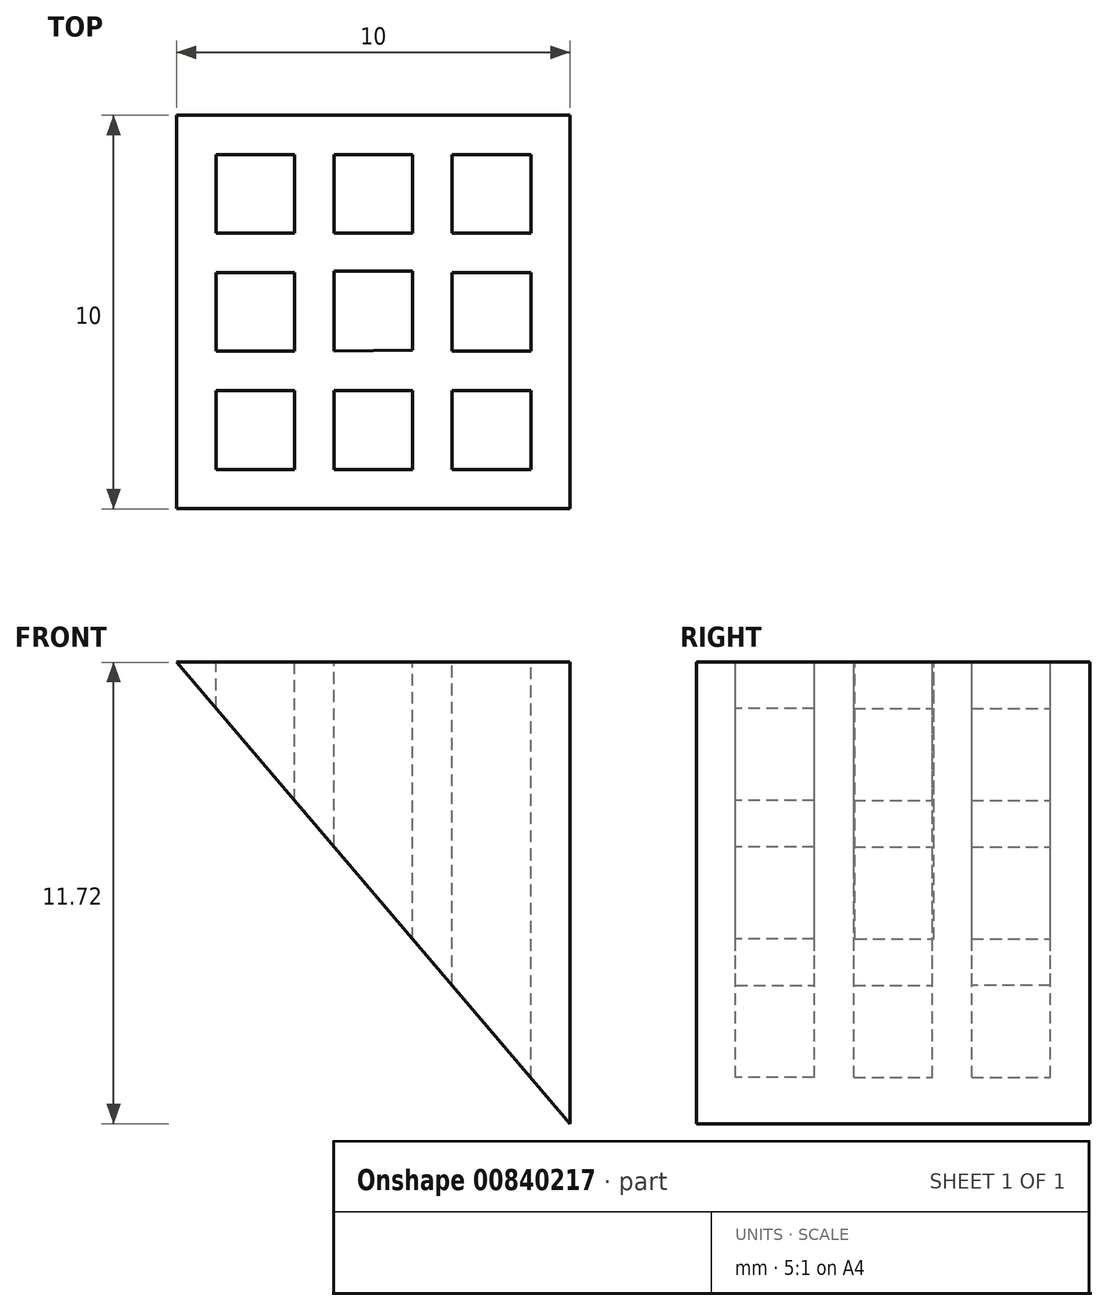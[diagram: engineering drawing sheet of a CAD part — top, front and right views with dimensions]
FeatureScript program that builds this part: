
annotation { "Feature Type Name" : "Feature", "Feature Type Description" : "" }
export const myFeature = defineFeature(function(context is Context, id is Id, definition is map)
    precondition{}
    {
        {
            var Q0;
            Q0=qCreatedBy(makeId("Top.planeOp"),FACE);
            var sketch = newSketch(context, id + "F0", { "sketchPlane" : qUnion([Q0])});
            skLineSegment(sketch, "E0", {"start": v(-23.24, 8.4) * mm, "end": v(-23.24, -1.6) * mm});
            skLineSegment(sketch, "E1", {"start": v(-23.24, 8.4) * mm, "end": v(-13.24, 8.4) * mm});
            skLineSegment(sketch, "E2", {"start": v(-23.24, -1.6) * mm, "end": v(-13.24, -1.6) * mm});
            skLineSegment(sketch, "E3", {"start": v(-13.24, 8.4) * mm, "end": v(-13.24, -1.6) * mm});
            skSolve(sketch);
        }
        {
            var Q0;
            Q0=makeQuery(id+"F0.imprint","IMPRINT",FACE,{"disambiguationData":[TD([[makeQuery(id+"F0.imprint","IMPRINT",EDGE,{"derivedFrom":sQuery(id+"F0.wireOp",EDGE,"E0")}),1.0]])]});
            extrude(context, id + "F1", {"entities" : qUnion([Q0]), "depth" : 577 * mm, "offsetDistance" : 25 * mm});
        }
        {
            var Q0;
            Q0=makeQuery(id+"F1.opExtrude","CAP_FACE",FACE,{"disambiguationData":[OSD([sQuery(id+"F0.wireOp",EDGE,"E0"),sQuery(id+"F0.wireOp",EDGE,"E1"),sQuery(id+"F0.wireOp",EDGE,"E2"),sQuery(id+"F0.wireOp",EDGE,"E3")])],"isStart":false});
            var sketch = newSketch(context, id + "F2", { "sketchPlane" : qUnion([Q0])});
            skLineSegment(sketch, "E4", {"start": v(-22.24, 7.4) * mm, "end": v(-22.24, 5.4) * mm});
            skLineSegment(sketch, "E5", {"start": v(-22.24, 7.4) * mm, "end": v(-20.24, 7.4) * mm});
            skLineSegment(sketch, "E6", {"start": v(-22.24, 5.4) * mm, "end": v(-20.24, 5.4) * mm});
            skLineSegment(sketch, "E7", {"start": v(-20.24, 7.4) * mm, "end": v(-20.24, 5.4) * mm});
            skLineSegment(sketch, "E8", {"start": v(-19.24, 7.4) * mm, "end": v(-19.24, 5.4) * mm});
            skLineSegment(sketch, "E9", {"start": v(-19.24, 5.4) * mm, "end": v(-17.24, 5.4) * mm});
            skLineSegment(sketch, "E10", {"start": v(-19.24, 7.4) * mm, "end": v(-17.24, 7.4) * mm});
            skLineSegment(sketch, "E11", {"start": v(-17.24, 7.4) * mm, "end": v(-17.24, 5.4) * mm});
            skLineSegment(sketch, "E12", {"start": v(-16.24, 5.4) * mm, "end": v(-16.24, 7.4) * mm});
            skLineSegment(sketch, "E13", {"start": v(-16.24, 5.4) * mm, "end": v(-14.24, 5.4) * mm});
            skLineSegment(sketch, "E14", {"start": v(-16.24, 7.4) * mm, "end": v(-14.24, 7.4) * mm});
            skLineSegment(sketch, "E15", {"start": v(-14.24, 7.4) * mm, "end": v(-14.24, 5.4) * mm});
            skLineSegment(sketch, "E16", {"start": v(-12.45, 8.4) * mm, "end": v(-12.45, 3.4) * mm});
            skLineSegment(sketch, "E17.MirrorCS", {"start": v(-19.24, 1.4) * mm, "end": v(-17.24, 1.4) * mm});
            skLineSegment(sketch, "E18.MirrorCS", {"start": v(-19.24, -0.6) * mm, "end": v(-19.24, 1.4) * mm});
            skLineSegment(sketch, "E19.MirrorCS", {"start": v(-19.24, -0.6) * mm, "end": v(-17.24, -0.6) * mm});
            skLineSegment(sketch, "E20.MirrorCS", {"start": v(-17.24, -0.6) * mm, "end": v(-17.24, 1.4) * mm});
            skLineSegment(sketch, "E21.MirrorCS", {"start": v(-16.24, 1.4) * mm, "end": v(-14.24, 1.4) * mm});
            skLineSegment(sketch, "E22.MirrorCS", {"start": v(-16.24, 1.4) * mm, "end": v(-16.24, -0.6) * mm});
            skLineSegment(sketch, "E23.MirrorCS", {"start": v(-14.24, -0.6) * mm, "end": v(-14.24, 1.4) * mm});
            skLineSegment(sketch, "E24.MirrorCS", {"start": v(-16.24, -0.6) * mm, "end": v(-14.24, -0.6) * mm});
            skLineSegment(sketch, "E25.MirrorCS", {"start": v(-22.24, 1.4) * mm, "end": v(-20.24, 1.4) * mm});
            skLineSegment(sketch, "E26.MirrorCS", {"start": v(-22.24, -0.6) * mm, "end": v(-22.24, 1.4) * mm});
            skLineSegment(sketch, "E27.MirrorCS", {"start": v(-22.24, -0.6) * mm, "end": v(-20.24, -0.6) * mm});
            skLineSegment(sketch, "E28.MirrorCS", {"start": v(-20.24, -0.6) * mm, "end": v(-20.24, 1.4) * mm});
            skSolve(sketch);
        }
        {
            var Q0;
            Q0=makeQuery(id+"F2.imprint","IMPRINT",FACE,{"disambiguationData":[TD([[makeQuery(id+"F2.imprint","IMPRINT",EDGE,{"derivedFrom":sQuery(id+"F2.wireOp",EDGE,"E4")}),1.0]])]});
            var Q1;
            Q1=makeQuery(id+"F2.imprint","IMPRINT",FACE,{"disambiguationData":[TD([[makeQuery(id+"F2.imprint","IMPRINT",EDGE,{"derivedFrom":sQuery(id+"F2.wireOp",EDGE,"E8")}),1.0]])]});
            var Q2;
            Q2=makeQuery(id+"F2.imprint","IMPRINT",FACE,{"disambiguationData":[TD([[makeQuery(id+"F2.imprint","IMPRINT",EDGE,{"derivedFrom":sQuery(id+"F2.wireOp",EDGE,"E12")}),-1.0]])]});
            var Q3;
            Q3=makeQuery(id+"F2.imprint","IMPRINT",FACE,{"disambiguationData":[TD([[makeQuery(id+"F2.imprint","IMPRINT",EDGE,{"derivedFrom":sQuery(id+"F2.wireOp",EDGE,"E21.MirrorCS")}),-1.0]])]});
            var Q4;
            Q4=makeQuery(id+"F2.imprint","IMPRINT",FACE,{"disambiguationData":[TD([[makeQuery(id+"F2.imprint","IMPRINT",EDGE,{"derivedFrom":sQuery(id+"F2.wireOp",EDGE,"E17.MirrorCS")}),-1.0]])]});
            var Q5;
            Q5=makeQuery(id+"F2.imprint","IMPRINT",FACE,{"disambiguationData":[TD([[makeQuery(id+"F2.imprint","IMPRINT",EDGE,{"derivedFrom":sQuery(id+"F2.wireOp",EDGE,"E25.MirrorCS")}),-1.0]])]});
            extrude(context, id + "F3", {"entities" : qUnion([Q0, Q1, Q2, Q3, Q4, Q5]), "operationType" : NewBodyOperationType.REMOVE, "endBound" : BoundingType.THROUGH_ALL, "oppositeDirection" : true, "depth" : 25 * mm, "offsetDistance" : 25 * mm});
        }
        {
            var Q0;
            Q0=makeQuery(id+"F1.opExtrude","CAP_FACE",FACE,{"disambiguationData":[OSD([sQuery(id+"F0.wireOp",EDGE,"E0"),sQuery(id+"F0.wireOp",EDGE,"E1"),sQuery(id+"F0.wireOp",EDGE,"E2"),sQuery(id+"F0.wireOp",EDGE,"E3")])],"isStart":false});
            var sketch = newSketch(context, id + "F4", { "sketchPlane" : qUnion([Q0])});
            skLineSegment(sketch, "E29", {"start": v(-22.24, 4.4) * mm, "end": v(-22.24, 2.4) * mm});
            skLineSegment(sketch, "E30", {"start": v(-22.24, 4.4) * mm, "end": v(-20.24, 4.4) * mm});
            skLineSegment(sketch, "E31", {"start": v(-20.24, 4.4) * mm, "end": v(-20.24, 2.4) * mm});
            skLineSegment(sketch, "E32", {"start": v(-22.24, 2.4) * mm, "end": v(-20.24, 2.4) * mm});
            skLineSegment(sketch, "E33", {"start": v(-19.24, 4.44) * mm, "end": v(-19.24, 2.4) * mm});
            skLineSegment(sketch, "E34", {"start": v(-19.24, 4.44) * mm, "end": v(-17.24, 4.44) * mm});
            skLineSegment(sketch, "E35", {"start": v(-17.24, 4.44) * mm, "end": v(-17.24, 2.44) * mm});
            skLineSegment(sketch, "E36", {"start": v(-19.24, 2.4) * mm, "end": v(-17.24, 2.44) * mm});
            skLineSegment(sketch, "E37", {"start": v(-16.24, 4.4) * mm, "end": v(-14.24, 4.4) * mm});
            skLineSegment(sketch, "E38", {"start": v(-16.24, 4.4) * mm, "end": v(-16.24, 2.4) * mm});
            skLineSegment(sketch, "E39", {"start": v(-16.24, 2.4) * mm, "end": v(-14.24, 2.4) * mm});
            skLineSegment(sketch, "E40", {"start": v(-14.24, 4.4) * mm, "end": v(-14.24, 2.4) * mm});
            skSolve(sketch);
        }
        {
            var Q0;
            Q0=makeQuery(id+"F4.imprint","IMPRINT",FACE,{"disambiguationData":[TD([[makeQuery(id+"F4.imprint","IMPRINT",EDGE,{"derivedFrom":sQuery(id+"F4.wireOp",EDGE,"E29")}),1.0]])]});
            var Q1;
            Q1=makeQuery(id+"F4.imprint","IMPRINT",FACE,{"disambiguationData":[TD([[makeQuery(id+"F4.imprint","IMPRINT",EDGE,{"derivedFrom":sQuery(id+"F4.wireOp",EDGE,"E33")}),1.0]])]});
            var Q2;
            Q2=makeQuery(id+"F4.imprint","IMPRINT",FACE,{"disambiguationData":[TD([[makeQuery(id+"F4.imprint","IMPRINT",EDGE,{"derivedFrom":sQuery(id+"F4.wireOp",EDGE,"E37")}),-1.0]])]});
            extrude(context, id + "F5", {"entities" : qUnion([Q0, Q1, Q2]), "operationType" : NewBodyOperationType.REMOVE, "endBound" : BoundingType.THROUGH_ALL, "oppositeDirection" : true, "depth" : 25 * mm, "offsetDistance" : 25 * mm});
        }
        {
            var Q0;
            Q0=makeQuery(id+"F1.opExtrude","CAP_FACE",FACE,{"disambiguationData":[OSD([sQuery(id+"F0.wireOp",EDGE,"E0"),sQuery(id+"F0.wireOp",EDGE,"E1"),sQuery(id+"F0.wireOp",EDGE,"E2"),sQuery(id+"F0.wireOp",EDGE,"E3")])],"isStart":false});
            extrude(context, id + "F6", {"entities" : qUnion([Q0]), "operationType" : NewBodyOperationType.REMOVE, "oppositeDirection" : true, "depth" : 500 * mm, "offsetDistance" : 25 * mm});
        }
        {
            var Q0;
            Q0=makeQuery(id+"F6.boolean.opBoolean","COPY",FACE,{"derivedFrom":makeQuery(id+"F6.opExtrude","CAP_FACE",FACE,{"disambiguationData":[OSD([sQuery(id+"F0.wireOp",EDGE,"E0"),sQuery(id+"F0.wireOp",EDGE,"E1"),sQuery(id+"F0.wireOp",EDGE,"E2"),sQuery(id+"F0.wireOp",EDGE,"E3")])],"isStart":false})});
            extrude(context, id + "F7", {"entities" : qUnion([Q0]), "operationType" : NewBodyOperationType.REMOVE, "oppositeDirection" : true, "depth" : 65.28 * mm, "offsetDistance" : 25 * mm});
        }
        {
            var Q0;
            Q0=makeQuery(id+"F1.opExtrude","SWEPT_FACE",FACE,{"disambiguationData":[OSD([sQuery(id+"F0.wireOp",EDGE,"E1")])]});
            var sketch = newSketch(context, id + "F8", { "sketchPlane" : qUnion([Q0])});
            skLineSegment(sketch, "E41", {"start": v(23.24, 11.72) * mm, "end": v(13.24, 0) * mm});
            skSolve(sketch);
        }
        {
            var Q0;
            Q0=makeQuery(id+"F8.imprint","IMPRINT",FACE,{"disambiguationData":[TD([[makeQuery(id+"F8.imprint","IMPRINT",EDGE,{"derivedFrom":sQuery(id+"F8.wireOp",EDGE,"E41")}),1.0]])]});
            extrude(context, id + "F9", {"entities" : qUnion([Q0]), "operationType" : NewBodyOperationType.REMOVE, "endBound" : BoundingType.THROUGH_ALL, "oppositeDirection" : true, "depth" : 25 * mm, "offsetDistance" : 25 * mm});
        }
    });
